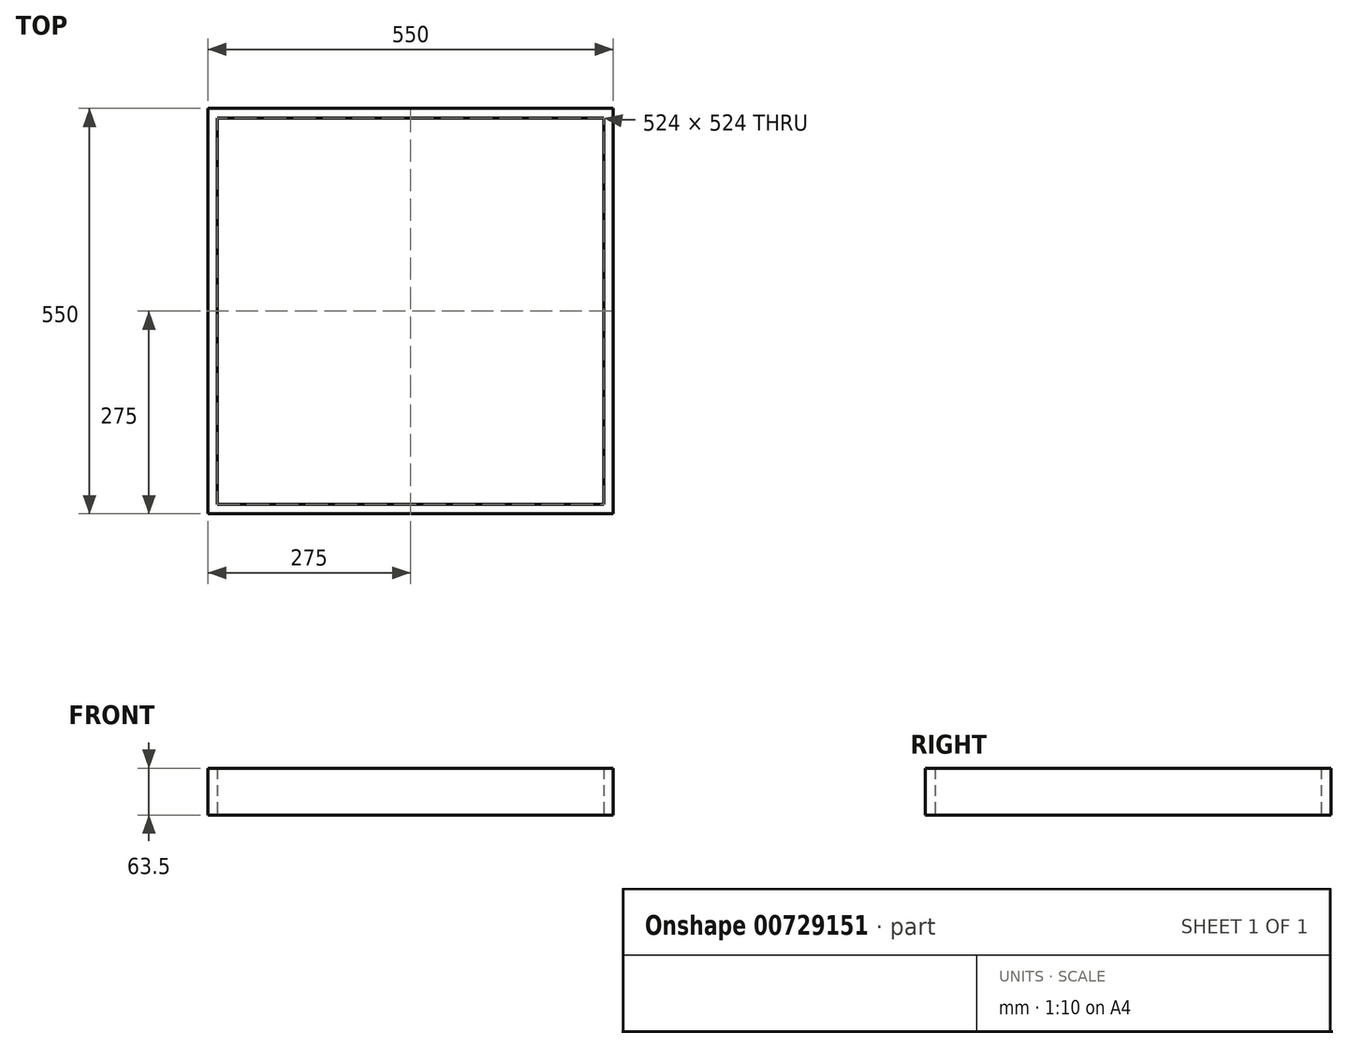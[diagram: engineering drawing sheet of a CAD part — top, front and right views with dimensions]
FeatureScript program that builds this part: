
annotation { "Feature Type Name" : "Feature", "Feature Type Description" : "" }
export const myFeature = defineFeature(function(context is Context, id is Id, definition is map)
    precondition{}
    {
        {
            var Q0;
            Q0=qCreatedBy(makeId("Top.planeOp"),FACE);
            var sketch = newSketch(context, id + "F0", { "sketchPlane" : qUnion([Q0])});
            skLineSegment(sketch, "E0.bottom", {"start": v(275, -275) * mm, "end": v(-275, -275) * mm});
            skLineSegment(sketch, "E0.top", {"start": v(275, 275) * mm, "end": v(-275, 275) * mm});
            skLineSegment(sketch, "E0.left", {"start": v(275, -275) * mm, "end": v(275, 275) * mm});
            skLineSegment(sketch, "E0.right", {"start": v(-275, -275) * mm, "end": v(-275, 275) * mm});
            skPoint(sketch, "E0.middle", {"position": v(0, 0) * mm});
            skLineSegment(sketch, "E1.bottom", {"start": v(262, -262) * mm, "end": v(-262, -262) * mm});
            skLineSegment(sketch, "E1.top", {"start": v(262, 262) * mm, "end": v(-262, 262) * mm});
            skLineSegment(sketch, "E1.left", {"start": v(262, -262) * mm, "end": v(262, 262) * mm});
            skLineSegment(sketch, "E1.right", {"start": v(-262, -262) * mm, "end": v(-262, 262) * mm});
            skSolve(sketch);
        }
        {
            var Q0;
            Q0=makeQuery(id+"F0.imprint","IMPRINT",FACE,{"disambiguationData":[TD([[makeQuery(id+"F0.imprint","IMPRINT",EDGE,{"derivedFrom":sQuery(id+"F0.wireOp",EDGE,"E0.bottom")}),-1.0]])]});
            extrude(context, id + "F1", {"entities" : qUnion([Q0]), "depth" : 63.5 * mm, "offsetDistance" : 25 * mm});
        }
    });
